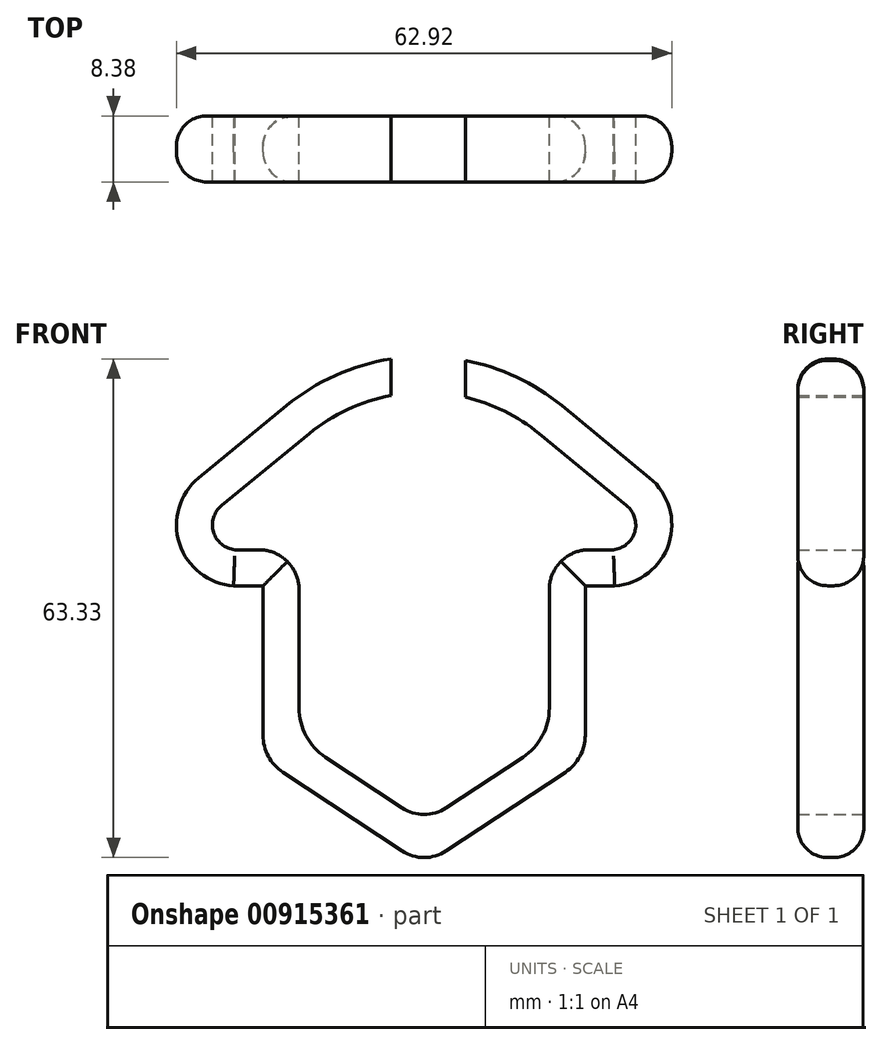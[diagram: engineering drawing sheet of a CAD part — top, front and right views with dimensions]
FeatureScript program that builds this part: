
annotation { "Feature Type Name" : "Feature", "Feature Type Description" : "" }
export const myFeature = defineFeature(function(context is Context, id is Id, definition is map)
    precondition{}
    {
        {
            var Q0;
            Q0=qCreatedBy(makeId("Front.planeOp"),FACE);
            var sketch = newSketch(context, id + "F0", { "sketchPlane" : qUnion([Q0])});
            skLineSegment(sketch, "E0", {"start": v(-15.9, 10.36) * mm, "end": v(-15.9, -13.77) * mm});
            skLineSegment(sketch, "E1", {"start": v(-15.9, -13.77) * mm, "end": v(0, -24.27) * mm});
            skLineSegment(sketch, "E2", {"start": v(-15.9, 10.36) * mm, "end": v(-24.02, 10.36) * mm});
            skLineSegment(sketch, "E3", {"start": v(-25.73, 15.97) * mm, "end": v(-14.59, 25.12) * mm});
            skArc(sketch, "E4", {"start": v(-25.73, 15.97) * mm, "mid": v(-26.75, 12.6) * mm, "end": v(-24.02, 10.36) * mm});
            skLineSegment(sketch, "E5.MirrorCS", {"start": v(15.9, 10.36) * mm, "end": v(15.9, -13.77) * mm});
            skLineSegment(sketch, "E6.MirrorCS", {"start": v(15.9, -13.77) * mm, "end": v(0, -24.27) * mm});
            skArc(sketch, "E7.MirrorCS", {"start": v(25.73, 15.97) * mm, "mid": v(26.75, 12.6) * mm, "end": v(24.02, 10.36) * mm});
            skLineSegment(sketch, "E8.MirrorCS", {"start": v(25.73, 15.97) * mm, "end": v(14.59, 25.12) * mm});
            skLineSegment(sketch, "E9.MirrorCS", {"start": v(15.9, 10.36) * mm, "end": v(24.02, 10.36) * mm});
            skArc(sketch, "E10", {"start": v(14.59, 25.12) * mm, "mid": v(0, 30.35) * mm, "end": v(-14.59, 25.12) * mm});
            skLineSegment(sketch, "E11.0", {"start": v(-20.47, 5.79) * mm, "end": v(-20.47, -16.23) * mm});
            skLineSegment(sketch, "E11.1", {"start": v(-20.47, 5.79) * mm, "end": v(-24.2, 5.79) * mm});
            skArc(sketch, "E11.2", {"start": v(-28.63, 19.5) * mm, "mid": v(-31.08, 11.14) * mm, "end": v(-24.2, 5.79) * mm});
            skLineSegment(sketch, "E11.3", {"start": v(-28.63, 19.5) * mm, "end": v(-17.49, 28.66) * mm});
            skArc(sketch, "E11.4", {"start": v(17.49, 28.66) * mm, "mid": v(0, 34.92) * mm, "end": v(-17.49, 28.66) * mm});
            skLineSegment(sketch, "E11.5", {"start": v(-20.47, -16.23) * mm, "end": v(0, -29.75) * mm});
            skLineSegment(sketch, "E11.6", {"start": v(20.47, -16.23) * mm, "end": v(0, -29.75) * mm});
            skLineSegment(sketch, "E11.7", {"start": v(20.47, 5.79) * mm, "end": v(20.47, -16.23) * mm});
            skLineSegment(sketch, "E11.8", {"start": v(20.47, 5.79) * mm, "end": v(24.2, 5.79) * mm});
            skArc(sketch, "E11.9", {"start": v(28.63, 19.5) * mm, "mid": v(31.08, 11.14) * mm, "end": v(24.2, 5.79) * mm});
            skLineSegment(sketch, "E11.10", {"start": v(28.63, 19.5) * mm, "end": v(17.49, 28.66) * mm});
            skSolve(sketch);
        }
        {
            var Q0;
            Q0 = qSketchRegion(id + "F0", true);
            extrude(context, id + "F1", {"entities" : qUnion([Q0]), "depth" : 8.38 * mm, "offsetDistance" : 25.4 * mm});
        }
        {
            var Q0;
            Q0=makeQuery(id+"F1.opExtrude","SWEPT_EDGE",EDGE,{"disambiguationData":[OSD([sQuery(id+"F0.wireOp",EDGE,"E11.5"),sQuery(id+"F0.wireOp",EDGE,"E11.6")])]});
            fillet(context, id + "F2", {"entities" : qUnion([Q0]), "radius" : 5.08 * mm, "tangentPropagation" : true, "allowEdgeOverflow" : false});
        }
        {
            var Q0;
            Q0=makeQuery(id+"F1.opExtrude","SWEPT_EDGE",EDGE,{"disambiguationData":[OSD([sQuery(id+"F0.wireOp",EDGE,"E11.6"),sQuery(id+"F0.wireOp",EDGE,"E11.7")])]});
            fillet(context, id + "F3", {"entities" : qUnion([Q0]), "radius" : 5.62 * mm, "tangentPropagation" : true, "allowEdgeOverflow" : false});
        }
        {
            var Q0;
            Q0=makeQuery(id+"F1.opExtrude","SWEPT_EDGE",EDGE,{"disambiguationData":[OSD([sQuery(id+"F0.wireOp",EDGE,"E11.0"),sQuery(id+"F0.wireOp",EDGE,"E11.5")])]});
            fillet(context, id + "F4", {"entities" : qUnion([Q0]), "radius" : 5.62 * mm, "tangentPropagation" : true, "allowEdgeOverflow" : false});
        }
        {
            var Q0;
            Q0=makeQuery(id+"F1.opExtrude","SWEPT_EDGE",EDGE,{"disambiguationData":[OSD([sQuery(id+"F0.wireOp",EDGE,"E5.MirrorCS"),sQuery(id+"F0.wireOp",EDGE,"E6.MirrorCS")])]});
            fillet(context, id + "F5", {"entities" : qUnion([Q0]), "radius" : 7.5 * mm, "tangentPropagation" : true, "allowEdgeOverflow" : false});
        }
        {
            var Q0;
            Q0=makeQuery(id+"F1.opExtrude","SWEPT_EDGE",EDGE,{"disambiguationData":[OSD([sQuery(id+"F0.wireOp",EDGE,"E0"),sQuery(id+"F0.wireOp",EDGE,"E1")])]});
            fillet(context, id + "F6", {"entities" : qUnion([Q0]), "radius" : 7.5 * mm, "tangentPropagation" : true, "allowEdgeOverflow" : false});
        }
        {
            var Q0;
            Q0=makeQuery(id+"F1.opExtrude","SWEPT_EDGE",EDGE,{"disambiguationData":[OSD([sQuery(id+"F0.wireOp",EDGE,"E1"),sQuery(id+"F0.wireOp",EDGE,"E6.MirrorCS")])]});
            fillet(context, id + "F7", {"entities" : qUnion([Q0]), "radius" : 5.08 * mm, "tangentPropagation" : true, "allowEdgeOverflow" : false});
        }
        {
            var Q0;
            Q0=makeQuery(id+"F1.opExtrude","SWEPT_EDGE",EDGE,{"disambiguationData":[OSD([sQuery(id+"F0.wireOp",EDGE,"E5.MirrorCS"),sQuery(id+"F0.wireOp",EDGE,"E9.MirrorCS")])]});
            fillet(context, id + "F8", {"entities" : qUnion([Q0]), "radius" : 5.08 * mm, "tangentPropagation" : true, "allowEdgeOverflow" : false});
        }
        {
            var Q0;
            Q0=makeQuery(id+"F1.opExtrude","SWEPT_EDGE",EDGE,{"disambiguationData":[OSD([sQuery(id+"F0.wireOp",EDGE,"E0"),sQuery(id+"F0.wireOp",EDGE,"E2")])]});
            fillet(context, id + "F9", {"entities" : qUnion([Q0]), "radius" : 5.08 * mm, "tangentPropagation" : true, "allowEdgeOverflow" : false});
        }
        {
            var Q0;
            Q0=makeQuery(id+"F1.opExtrude","CAP_EDGE",EDGE,{"disambiguationData":[OSD([sQuery(id+"F0.wireOp",EDGE,"E11.6")])],"isStart":false});
            var Q1;
            Q1=makeQuery(id+"F1.opExtrude","CAP_EDGE",EDGE,{"disambiguationData":[OSD([sQuery(id+"F0.wireOp",EDGE,"E11.5")])],"isStart":false});
            var Q2;
            Q2=makeQuery(id+"F1.opExtrude","CAP_EDGE",EDGE,{"disambiguationData":[OSD([sQuery(id+"F0.wireOp",EDGE,"E11.0")])],"isStart":false});
            var Q3;
            Q3=makeQuery(id+"F1.opExtrude","CAP_EDGE",EDGE,{"disambiguationData":[OSD([sQuery(id+"F0.wireOp",EDGE,"E11.1")])],"isStart":false});
            var Q4;
            Q4=makeQuery(id+"F1.opExtrude","CAP_EDGE",EDGE,{"disambiguationData":[OSD([sQuery(id+"F0.wireOp",EDGE,"E11.2")])],"isStart":false});
            var Q5;
            Q5=makeQuery(id+"F1.opExtrude","CAP_EDGE",EDGE,{"disambiguationData":[OSD([sQuery(id+"F0.wireOp",EDGE,"E11.3")])],"isStart":false});
            var Q6;
            {var subQ0=sQuery(id+"F0.wireOp",EDGE,"E11.5");var subQ1=sQuery(id+"F0.wireOp",EDGE,"E11.0");Q6=makeQuery(id+"F4.opFillet","BLEND_EDGE",EDGE,{"blendedFrom":[makeQuery(id+"F1.opExtrude","SWEPT_EDGE",EDGE,{"disambiguationData":[OSD([subQ1,subQ0])]}),makeQuery(id+"F1.opExtrude","CAP_FACE",FACE,{"disambiguationData":[OSD([sQuery(id+"F0.wireOp",EDGE,"E0"),sQuery(id+"F0.wireOp",EDGE,"E1"),sQuery(id+"F0.wireOp",EDGE,"E2"),sQuery(id+"F0.wireOp",EDGE,"E3"),sQuery(id+"F0.wireOp",EDGE,"E4"),sQuery(id+"F0.wireOp",EDGE,"E5.MirrorCS"),sQuery(id+"F0.wireOp",EDGE,"E6.MirrorCS"),sQuery(id+"F0.wireOp",EDGE,"E7.MirrorCS"),sQuery(id+"F0.wireOp",EDGE,"E8.MirrorCS"),sQuery(id+"F0.wireOp",EDGE,"E9.MirrorCS"),sQuery(id+"F0.wireOp",EDGE,"E10"),subQ1,sQuery(id+"F0.wireOp",EDGE,"E11.1"),sQuery(id+"F0.wireOp",EDGE,"E11.2"),sQuery(id+"F0.wireOp",EDGE,"E11.3"),sQuery(id+"F0.wireOp",EDGE,"E11.4"),subQ0,sQuery(id+"F0.wireOp",EDGE,"E11.6"),sQuery(id+"F0.wireOp",EDGE,"E11.7"),sQuery(id+"F0.wireOp",EDGE,"E11.8"),sQuery(id+"F0.wireOp",EDGE,"E11.9"),sQuery(id+"F0.wireOp",EDGE,"E11.10")])],"isStart":false})],"blendedInto":[makeQuery(id+"F1.opExtrude","CAP_FACE",FACE,{"disambiguationData":[OSD([sQuery(id+"F0.wireOp",EDGE,"E0"),sQuery(id+"F0.wireOp",EDGE,"E1"),sQuery(id+"F0.wireOp",EDGE,"E2"),sQuery(id+"F0.wireOp",EDGE,"E3"),sQuery(id+"F0.wireOp",EDGE,"E4"),sQuery(id+"F0.wireOp",EDGE,"E5.MirrorCS"),sQuery(id+"F0.wireOp",EDGE,"E6.MirrorCS"),sQuery(id+"F0.wireOp",EDGE,"E7.MirrorCS"),sQuery(id+"F0.wireOp",EDGE,"E8.MirrorCS"),sQuery(id+"F0.wireOp",EDGE,"E9.MirrorCS"),sQuery(id+"F0.wireOp",EDGE,"E10"),subQ1,sQuery(id+"F0.wireOp",EDGE,"E11.1"),sQuery(id+"F0.wireOp",EDGE,"E11.2"),sQuery(id+"F0.wireOp",EDGE,"E11.3"),sQuery(id+"F0.wireOp",EDGE,"E11.4"),subQ0,sQuery(id+"F0.wireOp",EDGE,"E11.6"),sQuery(id+"F0.wireOp",EDGE,"E11.7"),sQuery(id+"F0.wireOp",EDGE,"E11.8"),sQuery(id+"F0.wireOp",EDGE,"E11.9"),sQuery(id+"F0.wireOp",EDGE,"E11.10")])],"isStart":false})]});}
            var Q7;
            {var subQ0=sQuery(id+"F0.wireOp",EDGE,"E11.6");var subQ1=sQuery(id+"F0.wireOp",EDGE,"E11.5");Q7=makeQuery(id+"F2.opFillet","BLEND_EDGE",EDGE,{"blendedFrom":[makeQuery(id+"F1.opExtrude","SWEPT_EDGE",EDGE,{"disambiguationData":[OSD([subQ1,subQ0])]}),makeQuery(id+"F1.opExtrude","CAP_FACE",FACE,{"disambiguationData":[OSD([sQuery(id+"F0.wireOp",EDGE,"E0"),sQuery(id+"F0.wireOp",EDGE,"E1"),sQuery(id+"F0.wireOp",EDGE,"E2"),sQuery(id+"F0.wireOp",EDGE,"E3"),sQuery(id+"F0.wireOp",EDGE,"E4"),sQuery(id+"F0.wireOp",EDGE,"E5.MirrorCS"),sQuery(id+"F0.wireOp",EDGE,"E6.MirrorCS"),sQuery(id+"F0.wireOp",EDGE,"E7.MirrorCS"),sQuery(id+"F0.wireOp",EDGE,"E8.MirrorCS"),sQuery(id+"F0.wireOp",EDGE,"E9.MirrorCS"),sQuery(id+"F0.wireOp",EDGE,"E10"),sQuery(id+"F0.wireOp",EDGE,"E11.0"),sQuery(id+"F0.wireOp",EDGE,"E11.1"),sQuery(id+"F0.wireOp",EDGE,"E11.2"),sQuery(id+"F0.wireOp",EDGE,"E11.3"),sQuery(id+"F0.wireOp",EDGE,"E11.4"),subQ1,subQ0,sQuery(id+"F0.wireOp",EDGE,"E11.7"),sQuery(id+"F0.wireOp",EDGE,"E11.8"),sQuery(id+"F0.wireOp",EDGE,"E11.9"),sQuery(id+"F0.wireOp",EDGE,"E11.10")])],"isStart":false})],"blendedInto":[makeQuery(id+"F1.opExtrude","CAP_FACE",FACE,{"disambiguationData":[OSD([sQuery(id+"F0.wireOp",EDGE,"E0"),sQuery(id+"F0.wireOp",EDGE,"E1"),sQuery(id+"F0.wireOp",EDGE,"E2"),sQuery(id+"F0.wireOp",EDGE,"E3"),sQuery(id+"F0.wireOp",EDGE,"E4"),sQuery(id+"F0.wireOp",EDGE,"E5.MirrorCS"),sQuery(id+"F0.wireOp",EDGE,"E6.MirrorCS"),sQuery(id+"F0.wireOp",EDGE,"E7.MirrorCS"),sQuery(id+"F0.wireOp",EDGE,"E8.MirrorCS"),sQuery(id+"F0.wireOp",EDGE,"E9.MirrorCS"),sQuery(id+"F0.wireOp",EDGE,"E10"),sQuery(id+"F0.wireOp",EDGE,"E11.0"),sQuery(id+"F0.wireOp",EDGE,"E11.1"),sQuery(id+"F0.wireOp",EDGE,"E11.2"),sQuery(id+"F0.wireOp",EDGE,"E11.3"),sQuery(id+"F0.wireOp",EDGE,"E11.4"),subQ1,subQ0,sQuery(id+"F0.wireOp",EDGE,"E11.7"),sQuery(id+"F0.wireOp",EDGE,"E11.8"),sQuery(id+"F0.wireOp",EDGE,"E11.9"),sQuery(id+"F0.wireOp",EDGE,"E11.10")])],"isStart":false})]});}
            var Q8;
            {var subQ0=sQuery(id+"F0.wireOp",EDGE,"E11.7");var subQ1=sQuery(id+"F0.wireOp",EDGE,"E11.6");Q8=makeQuery(id+"F3.opFillet","BLEND_EDGE",EDGE,{"blendedFrom":[makeQuery(id+"F1.opExtrude","SWEPT_EDGE",EDGE,{"disambiguationData":[OSD([subQ1,subQ0])]}),makeQuery(id+"F1.opExtrude","CAP_FACE",FACE,{"disambiguationData":[OSD([sQuery(id+"F0.wireOp",EDGE,"E0"),sQuery(id+"F0.wireOp",EDGE,"E1"),sQuery(id+"F0.wireOp",EDGE,"E2"),sQuery(id+"F0.wireOp",EDGE,"E3"),sQuery(id+"F0.wireOp",EDGE,"E4"),sQuery(id+"F0.wireOp",EDGE,"E5.MirrorCS"),sQuery(id+"F0.wireOp",EDGE,"E6.MirrorCS"),sQuery(id+"F0.wireOp",EDGE,"E7.MirrorCS"),sQuery(id+"F0.wireOp",EDGE,"E8.MirrorCS"),sQuery(id+"F0.wireOp",EDGE,"E9.MirrorCS"),sQuery(id+"F0.wireOp",EDGE,"E10"),sQuery(id+"F0.wireOp",EDGE,"E11.0"),sQuery(id+"F0.wireOp",EDGE,"E11.1"),sQuery(id+"F0.wireOp",EDGE,"E11.2"),sQuery(id+"F0.wireOp",EDGE,"E11.3"),sQuery(id+"F0.wireOp",EDGE,"E11.4"),sQuery(id+"F0.wireOp",EDGE,"E11.5"),subQ1,subQ0,sQuery(id+"F0.wireOp",EDGE,"E11.8"),sQuery(id+"F0.wireOp",EDGE,"E11.9"),sQuery(id+"F0.wireOp",EDGE,"E11.10")])],"isStart":false})],"blendedInto":[makeQuery(id+"F1.opExtrude","CAP_FACE",FACE,{"disambiguationData":[OSD([sQuery(id+"F0.wireOp",EDGE,"E0"),sQuery(id+"F0.wireOp",EDGE,"E1"),sQuery(id+"F0.wireOp",EDGE,"E2"),sQuery(id+"F0.wireOp",EDGE,"E3"),sQuery(id+"F0.wireOp",EDGE,"E4"),sQuery(id+"F0.wireOp",EDGE,"E5.MirrorCS"),sQuery(id+"F0.wireOp",EDGE,"E6.MirrorCS"),sQuery(id+"F0.wireOp",EDGE,"E7.MirrorCS"),sQuery(id+"F0.wireOp",EDGE,"E8.MirrorCS"),sQuery(id+"F0.wireOp",EDGE,"E9.MirrorCS"),sQuery(id+"F0.wireOp",EDGE,"E10"),sQuery(id+"F0.wireOp",EDGE,"E11.0"),sQuery(id+"F0.wireOp",EDGE,"E11.1"),sQuery(id+"F0.wireOp",EDGE,"E11.2"),sQuery(id+"F0.wireOp",EDGE,"E11.3"),sQuery(id+"F0.wireOp",EDGE,"E11.4"),sQuery(id+"F0.wireOp",EDGE,"E11.5"),subQ1,subQ0,sQuery(id+"F0.wireOp",EDGE,"E11.8"),sQuery(id+"F0.wireOp",EDGE,"E11.9"),sQuery(id+"F0.wireOp",EDGE,"E11.10")])],"isStart":false})]});}
            var Q9;
            Q9=makeQuery(id+"F1.opExtrude","CAP_EDGE",EDGE,{"disambiguationData":[OSD([sQuery(id+"F0.wireOp",EDGE,"E11.7")])],"isStart":false});
            var Q10;
            Q10=makeQuery(id+"F1.opExtrude","CAP_EDGE",EDGE,{"disambiguationData":[OSD([sQuery(id+"F0.wireOp",EDGE,"E11.8")])],"isStart":false});
            var Q11;
            Q11=makeQuery(id+"F1.opExtrude","CAP_EDGE",EDGE,{"disambiguationData":[OSD([sQuery(id+"F0.wireOp",EDGE,"E11.9")])],"isStart":false});
            var Q12;
            Q12=makeQuery(id+"F1.opExtrude","CAP_EDGE",EDGE,{"disambiguationData":[OSD([sQuery(id+"F0.wireOp",EDGE,"E11.10")])],"isStart":false});
            fillet(context, id + "F10", {"entities" : qUnion([Q0, Q1, Q2, Q3, Q4, Q5, Q6, Q7, Q8, Q9, Q10, Q11, Q12]), "radius" : 3.8 * mm, "tangentPropagation" : true, "allowEdgeOverflow" : false});
        }
        {
            var Q0;
            {var subQ0=sQuery(id+"F0.wireOp",EDGE,"E11.6");var subQ1=sQuery(id+"F0.wireOp",EDGE,"E11.5");Q0=makeQuery(id+"F2.opFillet","BLEND_EDGE",EDGE,{"blendedFrom":[makeQuery(id+"F1.opExtrude","SWEPT_EDGE",EDGE,{"disambiguationData":[OSD([subQ1,subQ0])]}),makeQuery(id+"F1.opExtrude","CAP_FACE",FACE,{"disambiguationData":[OSD([sQuery(id+"F0.wireOp",EDGE,"E0"),sQuery(id+"F0.wireOp",EDGE,"E1"),sQuery(id+"F0.wireOp",EDGE,"E2"),sQuery(id+"F0.wireOp",EDGE,"E3"),sQuery(id+"F0.wireOp",EDGE,"E4"),sQuery(id+"F0.wireOp",EDGE,"E5.MirrorCS"),sQuery(id+"F0.wireOp",EDGE,"E6.MirrorCS"),sQuery(id+"F0.wireOp",EDGE,"E7.MirrorCS"),sQuery(id+"F0.wireOp",EDGE,"E8.MirrorCS"),sQuery(id+"F0.wireOp",EDGE,"E9.MirrorCS"),sQuery(id+"F0.wireOp",EDGE,"E10"),sQuery(id+"F0.wireOp",EDGE,"E11.0"),sQuery(id+"F0.wireOp",EDGE,"E11.1"),sQuery(id+"F0.wireOp",EDGE,"E11.2"),sQuery(id+"F0.wireOp",EDGE,"E11.3"),sQuery(id+"F0.wireOp",EDGE,"E11.4"),subQ1,subQ0,sQuery(id+"F0.wireOp",EDGE,"E11.7"),sQuery(id+"F0.wireOp",EDGE,"E11.8"),sQuery(id+"F0.wireOp",EDGE,"E11.9"),sQuery(id+"F0.wireOp",EDGE,"E11.10")])],"isStart":true})],"blendedInto":[makeQuery(id+"F1.opExtrude","CAP_FACE",FACE,{"disambiguationData":[OSD([sQuery(id+"F0.wireOp",EDGE,"E0"),sQuery(id+"F0.wireOp",EDGE,"E1"),sQuery(id+"F0.wireOp",EDGE,"E2"),sQuery(id+"F0.wireOp",EDGE,"E3"),sQuery(id+"F0.wireOp",EDGE,"E4"),sQuery(id+"F0.wireOp",EDGE,"E5.MirrorCS"),sQuery(id+"F0.wireOp",EDGE,"E6.MirrorCS"),sQuery(id+"F0.wireOp",EDGE,"E7.MirrorCS"),sQuery(id+"F0.wireOp",EDGE,"E8.MirrorCS"),sQuery(id+"F0.wireOp",EDGE,"E9.MirrorCS"),sQuery(id+"F0.wireOp",EDGE,"E10"),sQuery(id+"F0.wireOp",EDGE,"E11.0"),sQuery(id+"F0.wireOp",EDGE,"E11.1"),sQuery(id+"F0.wireOp",EDGE,"E11.2"),sQuery(id+"F0.wireOp",EDGE,"E11.3"),sQuery(id+"F0.wireOp",EDGE,"E11.4"),subQ1,subQ0,sQuery(id+"F0.wireOp",EDGE,"E11.7"),sQuery(id+"F0.wireOp",EDGE,"E11.8"),sQuery(id+"F0.wireOp",EDGE,"E11.9"),sQuery(id+"F0.wireOp",EDGE,"E11.10")])],"isStart":true})]});}
            var Q1;
            Q1=makeQuery(id+"F1.opExtrude","CAP_EDGE",EDGE,{"disambiguationData":[OSD([sQuery(id+"F0.wireOp",EDGE,"E11.6")])],"isStart":true});
            var Q2;
            Q2=makeQuery(id+"F1.opExtrude","CAP_EDGE",EDGE,{"disambiguationData":[OSD([sQuery(id+"F0.wireOp",EDGE,"E11.10")])],"isStart":true});
            var Q3;
            Q3=makeQuery(id+"F1.opExtrude","CAP_EDGE",EDGE,{"disambiguationData":[OSD([sQuery(id+"F0.wireOp",EDGE,"E11.9")])],"isStart":true});
            var Q4;
            Q4=makeQuery(id+"F1.opExtrude","CAP_EDGE",EDGE,{"disambiguationData":[OSD([sQuery(id+"F0.wireOp",EDGE,"E11.7")])],"isStart":true});
            var Q5;
            Q5=makeQuery(id+"F1.opExtrude","CAP_EDGE",EDGE,{"disambiguationData":[OSD([sQuery(id+"F0.wireOp",EDGE,"E11.8")])],"isStart":true});
            var Q6;
            {var subQ0=sQuery(id+"F0.wireOp",EDGE,"E11.7");var subQ1=sQuery(id+"F0.wireOp",EDGE,"E11.6");Q6=makeQuery(id+"F3.opFillet","BLEND_EDGE",EDGE,{"blendedFrom":[makeQuery(id+"F1.opExtrude","SWEPT_EDGE",EDGE,{"disambiguationData":[OSD([subQ1,subQ0])]}),makeQuery(id+"F1.opExtrude","CAP_FACE",FACE,{"disambiguationData":[OSD([sQuery(id+"F0.wireOp",EDGE,"E0"),sQuery(id+"F0.wireOp",EDGE,"E1"),sQuery(id+"F0.wireOp",EDGE,"E2"),sQuery(id+"F0.wireOp",EDGE,"E3"),sQuery(id+"F0.wireOp",EDGE,"E4"),sQuery(id+"F0.wireOp",EDGE,"E5.MirrorCS"),sQuery(id+"F0.wireOp",EDGE,"E6.MirrorCS"),sQuery(id+"F0.wireOp",EDGE,"E7.MirrorCS"),sQuery(id+"F0.wireOp",EDGE,"E8.MirrorCS"),sQuery(id+"F0.wireOp",EDGE,"E9.MirrorCS"),sQuery(id+"F0.wireOp",EDGE,"E10"),sQuery(id+"F0.wireOp",EDGE,"E11.0"),sQuery(id+"F0.wireOp",EDGE,"E11.1"),sQuery(id+"F0.wireOp",EDGE,"E11.2"),sQuery(id+"F0.wireOp",EDGE,"E11.3"),sQuery(id+"F0.wireOp",EDGE,"E11.4"),sQuery(id+"F0.wireOp",EDGE,"E11.5"),subQ1,subQ0,sQuery(id+"F0.wireOp",EDGE,"E11.8"),sQuery(id+"F0.wireOp",EDGE,"E11.9"),sQuery(id+"F0.wireOp",EDGE,"E11.10")])],"isStart":true})],"blendedInto":[makeQuery(id+"F1.opExtrude","CAP_FACE",FACE,{"disambiguationData":[OSD([sQuery(id+"F0.wireOp",EDGE,"E0"),sQuery(id+"F0.wireOp",EDGE,"E1"),sQuery(id+"F0.wireOp",EDGE,"E2"),sQuery(id+"F0.wireOp",EDGE,"E3"),sQuery(id+"F0.wireOp",EDGE,"E4"),sQuery(id+"F0.wireOp",EDGE,"E5.MirrorCS"),sQuery(id+"F0.wireOp",EDGE,"E6.MirrorCS"),sQuery(id+"F0.wireOp",EDGE,"E7.MirrorCS"),sQuery(id+"F0.wireOp",EDGE,"E8.MirrorCS"),sQuery(id+"F0.wireOp",EDGE,"E9.MirrorCS"),sQuery(id+"F0.wireOp",EDGE,"E10"),sQuery(id+"F0.wireOp",EDGE,"E11.0"),sQuery(id+"F0.wireOp",EDGE,"E11.1"),sQuery(id+"F0.wireOp",EDGE,"E11.2"),sQuery(id+"F0.wireOp",EDGE,"E11.3"),sQuery(id+"F0.wireOp",EDGE,"E11.4"),sQuery(id+"F0.wireOp",EDGE,"E11.5"),subQ1,subQ0,sQuery(id+"F0.wireOp",EDGE,"E11.8"),sQuery(id+"F0.wireOp",EDGE,"E11.9"),sQuery(id+"F0.wireOp",EDGE,"E11.10")])],"isStart":true})]});}
            var Q7;
            Q7=makeQuery(id+"F1.opExtrude","CAP_EDGE",EDGE,{"disambiguationData":[OSD([sQuery(id+"F0.wireOp",EDGE,"E11.5")])],"isStart":true});
            var Q8;
            Q8=makeQuery(id+"F1.opExtrude","CAP_EDGE",EDGE,{"disambiguationData":[OSD([sQuery(id+"F0.wireOp",EDGE,"E11.0")])],"isStart":true});
            var Q9;
            Q9=makeQuery(id+"F1.opExtrude","CAP_EDGE",EDGE,{"disambiguationData":[OSD([sQuery(id+"F0.wireOp",EDGE,"E11.1")])],"isStart":true});
            var Q10;
            Q10=makeQuery(id+"F1.opExtrude","CAP_EDGE",EDGE,{"disambiguationData":[OSD([sQuery(id+"F0.wireOp",EDGE,"E11.2")])],"isStart":true});
            var Q11;
            Q11=makeQuery(id+"F1.opExtrude","CAP_EDGE",EDGE,{"disambiguationData":[OSD([sQuery(id+"F0.wireOp",EDGE,"E11.3")])],"isStart":true});
            var Q12;
            Q12=makeQuery(id+"F1.opExtrude","CAP_EDGE",EDGE,{"disambiguationData":[OSD([sQuery(id+"F0.wireOp",EDGE,"E11.4")])],"isStart":true});
            var Q13;
            {var subQ0=sQuery(id+"F0.wireOp",EDGE,"E11.5");var subQ1=sQuery(id+"F0.wireOp",EDGE,"E11.0");Q13=makeQuery(id+"F4.opFillet","BLEND_EDGE",EDGE,{"blendedFrom":[makeQuery(id+"F1.opExtrude","SWEPT_EDGE",EDGE,{"disambiguationData":[OSD([subQ1,subQ0])]}),makeQuery(id+"F1.opExtrude","CAP_FACE",FACE,{"disambiguationData":[OSD([sQuery(id+"F0.wireOp",EDGE,"E0"),sQuery(id+"F0.wireOp",EDGE,"E1"),sQuery(id+"F0.wireOp",EDGE,"E2"),sQuery(id+"F0.wireOp",EDGE,"E3"),sQuery(id+"F0.wireOp",EDGE,"E4"),sQuery(id+"F0.wireOp",EDGE,"E5.MirrorCS"),sQuery(id+"F0.wireOp",EDGE,"E6.MirrorCS"),sQuery(id+"F0.wireOp",EDGE,"E7.MirrorCS"),sQuery(id+"F0.wireOp",EDGE,"E8.MirrorCS"),sQuery(id+"F0.wireOp",EDGE,"E9.MirrorCS"),sQuery(id+"F0.wireOp",EDGE,"E10"),subQ1,sQuery(id+"F0.wireOp",EDGE,"E11.1"),sQuery(id+"F0.wireOp",EDGE,"E11.2"),sQuery(id+"F0.wireOp",EDGE,"E11.3"),sQuery(id+"F0.wireOp",EDGE,"E11.4"),subQ0,sQuery(id+"F0.wireOp",EDGE,"E11.6"),sQuery(id+"F0.wireOp",EDGE,"E11.7"),sQuery(id+"F0.wireOp",EDGE,"E11.8"),sQuery(id+"F0.wireOp",EDGE,"E11.9"),sQuery(id+"F0.wireOp",EDGE,"E11.10")])],"isStart":true})],"blendedInto":[makeQuery(id+"F1.opExtrude","CAP_FACE",FACE,{"disambiguationData":[OSD([sQuery(id+"F0.wireOp",EDGE,"E0"),sQuery(id+"F0.wireOp",EDGE,"E1"),sQuery(id+"F0.wireOp",EDGE,"E2"),sQuery(id+"F0.wireOp",EDGE,"E3"),sQuery(id+"F0.wireOp",EDGE,"E4"),sQuery(id+"F0.wireOp",EDGE,"E5.MirrorCS"),sQuery(id+"F0.wireOp",EDGE,"E6.MirrorCS"),sQuery(id+"F0.wireOp",EDGE,"E7.MirrorCS"),sQuery(id+"F0.wireOp",EDGE,"E8.MirrorCS"),sQuery(id+"F0.wireOp",EDGE,"E9.MirrorCS"),sQuery(id+"F0.wireOp",EDGE,"E10"),subQ1,sQuery(id+"F0.wireOp",EDGE,"E11.1"),sQuery(id+"F0.wireOp",EDGE,"E11.2"),sQuery(id+"F0.wireOp",EDGE,"E11.3"),sQuery(id+"F0.wireOp",EDGE,"E11.4"),subQ0,sQuery(id+"F0.wireOp",EDGE,"E11.6"),sQuery(id+"F0.wireOp",EDGE,"E11.7"),sQuery(id+"F0.wireOp",EDGE,"E11.8"),sQuery(id+"F0.wireOp",EDGE,"E11.9"),sQuery(id+"F0.wireOp",EDGE,"E11.10")])],"isStart":true})]});}
            fillet(context, id + "F11", {"entities" : qUnion([Q0, Q1, Q2, Q3, Q4, Q5, Q6, Q7, Q8, Q9, Q10, Q11, Q12, Q13]), "radius" : 3.8 * mm, "tangentPropagation" : true, "allowEdgeOverflow" : false});
        }
        {
            var Q0;
            Q0=qCreatedBy(makeId("Front.planeOp"),FACE);
            var sketch = newSketch(context, id + "F12", { "sketchPlane" : qUnion([Q0])});
            skLineSegment(sketch, "E12.bottom", {"start": v(5.25, 39.27) * mm, "end": v(-4.22, 39.27) * mm});
            skLineSegment(sketch, "E12.top", {"start": v(5.25, 24.56) * mm, "end": v(-4.22, 24.56) * mm});
            skLineSegment(sketch, "E12.left", {"start": v(5.25, 39.27) * mm, "end": v(5.25, 24.56) * mm});
            skLineSegment(sketch, "E12.right", {"start": v(-4.22, 39.27) * mm, "end": v(-4.22, 24.56) * mm});
            skSolve(sketch);
        }
        {
            var Q0;
            Q0 = qSketchRegion(id + "F12", true);
            extrude(context, id + "F13", {"entities" : qUnion([Q0]), "operationType" : NewBodyOperationType.REMOVE, "depth" : 10.16 * mm, "offsetDistance" : 25.4 * mm});
        }
    });
